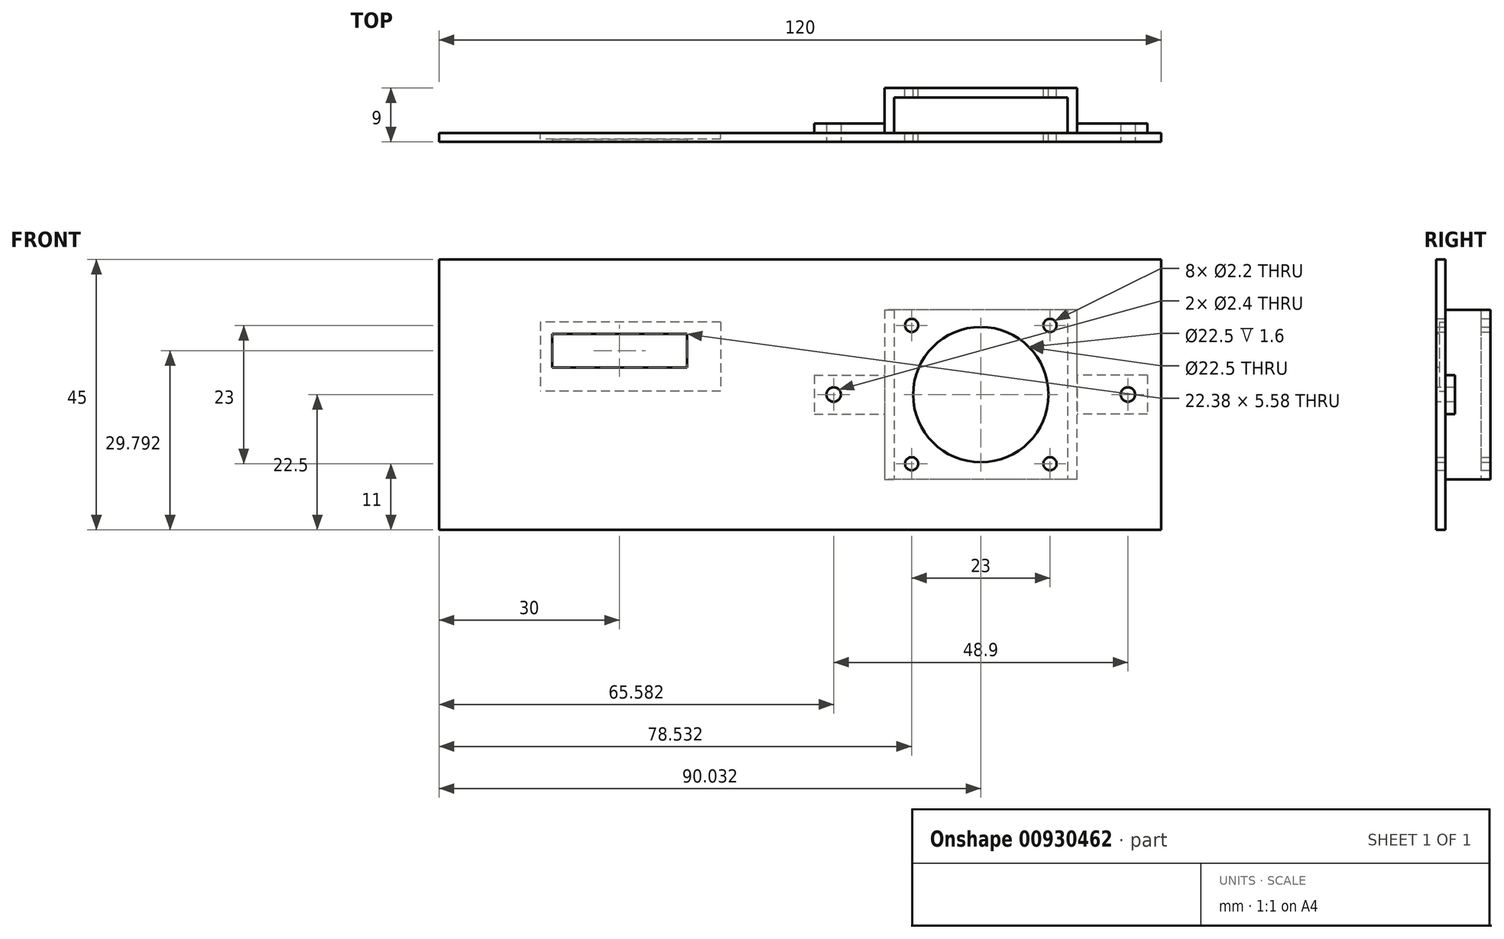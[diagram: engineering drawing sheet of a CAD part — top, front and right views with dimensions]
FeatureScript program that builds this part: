
annotation { "Feature Type Name" : "Feature", "Feature Type Description" : "" }
export const myFeature = defineFeature(function(context is Context, id is Id, definition is map)
    precondition{}
    {
        {
            var Q0;
            Q0=qCreatedBy(makeId("Top.planeOp"),FACE);
            var sketch = newSketch(context, id + "F0", { "sketchPlane" : qUnion([Q0])});
            skLineSegment(sketch, "E0.bottom", {"start": v(60, 0.75) * mm, "end": v(-60, 0.75) * mm});
            skLineSegment(sketch, "E0.top", {"start": v(60, -0.75) * mm, "end": v(-60, -0.75) * mm});
            skLineSegment(sketch, "E0.left", {"start": v(60, 0.75) * mm, "end": v(60, -0.75) * mm});
            skLineSegment(sketch, "E0.right", {"start": v(-60, 0.75) * mm, "end": v(-60, -0.75) * mm});
            skPoint(sketch, "E0.middle", {"position": v(0, 0) * mm});
            skSolve(sketch);
        }
        {
            var Q0;
            Q0 = qSketchRegion(id + "F0", true);
            extrude(context, id + "F1", {"entities" : qUnion([Q0]), "depth" : 45 * mm, "offsetDistance" : 25 * mm});
        }
        {
            var Q0;
            Q0=makeQuery(id+"F1.opExtrude","SWEPT_FACE",FACE,{"disambiguationData":[OSD([sQuery(id+"F0.wireOp",EDGE,"E0.top")])]});
            var sketch = newSketch(context, id + "F2", { "sketchPlane" : qUnion([Q0])});
            skCircle(sketch, "E1", {"center": v(30.03, 22.5) * mm, "radius": 4 * mm});
            skPoint(sketch, "E1.centerSnap0", {"position": v(60, 22.5) * mm});
            skSolve(sketch);
        }
        {
            var Q0;
            Q0=makeQuery(id+"F2.imprint","IMPRINT",FACE,{"disambiguationData":[TD([[makeQuery(id+"F2.imprint","IMPRINT",EDGE,{"derivedFrom":sQuery(id+"F2.wireOp",EDGE,"E1")}),1.0]])]});
            extrude(context, id + "F3", {"entities" : qUnion([Q0]), "operationType" : NewBodyOperationType.REMOVE, "oppositeDirection" : true, "depth" : 25 * mm, "offsetDistance" : 25 * mm});
        }
        {
            var Q0;
            Q0=makeQuery(id+"F1.opExtrude","SWEPT_FACE",FACE,{"disambiguationData":[OSD([sQuery(id+"F0.wireOp",EDGE,"E0.top")])]});
            var sketch = newSketch(context, id + "F4", { "sketchPlane" : qUnion([Q0])});
            skCircle(sketch, "E2", {"center": v(5.58, 22.5) * mm, "radius": 1.2 * mm});
            skCircle(sketch, "E3", {"center": v(54.48, 22.5) * mm, "radius": 1.2 * mm});
            skPoint(sketch, "E4", {"position": v(30.03, 22.5) * mm});
            skLineSegment(sketch, "E5", {"start": v(30.03, 26.5) * mm, "end": v(30.03, 18.5) * mm, "construction": true});
            skSolve(sketch);
        }
        {
            var Q0;
            Q0 = qSketchRegion(id + "F4", true);
            extrude(context, id + "F5", {"entities" : qUnion([Q0]), "operationType" : NewBodyOperationType.REMOVE, "oppositeDirection" : true, "depth" : 25 * mm, "offsetDistance" : 25 * mm});
        }
        {
            var Q0;
            Q0=makeQuery(id+"F1.opExtrude","SWEPT_FACE",FACE,{"disambiguationData":[OSD([sQuery(id+"F0.wireOp",EDGE,"E0.bottom")])]});
            var sketch = newSketch(context, id + "F6", { "sketchPlane" : qUnion([Q0])});
            skLineSegment(sketch, "E6.bottom", {"start": v(-57.73, 25.75) * mm, "end": v(-46.03, 25.75) * mm});
            skLineSegment(sketch, "E6.top", {"start": v(-57.73, 19.25) * mm, "end": v(-46.03, 19.25) * mm});
            skLineSegment(sketch, "E6.left", {"start": v(-57.73, 25.75) * mm, "end": v(-57.73, 19.25) * mm});
            skPoint(sketch, "E7", {"position": v(-30.03, 22.5) * mm});
            skLineSegment(sketch, "E8", {"start": v(-30.03, 26.5) * mm, "end": v(-30.03, 26.5) * mm});
            skLineSegment(sketch, "E9", {"start": v(-46.03, 25.75) * mm, "end": v(-46.03, 36.6) * mm});
            skLineSegment(sketch, "E10", {"start": v(-46.03, 36.6) * mm, "end": v(-44.43, 36.6) * mm});
            skLineSegment(sketch, "E11", {"start": v(-46.03, 19.25) * mm, "end": v(-46.03, 8.4) * mm});
            skLineSegment(sketch, "E12", {"start": v(-46.03, 8.4) * mm, "end": v(-44.43, 8.4) * mm});
            skLineSegment(sketch, "E13", {"start": v(-46.03, 25.75) * mm, "end": v(-46.03, 19.25) * mm});
            skPoint(sketch, "E14", {"position": v(-54.48, 22.5) * mm});
            skPoint(sketch, "E15", {"position": v(-57.73, 22.5) * mm});
            skLineSegment(sketch, "E16", {"start": v(-44.43, 36.6) * mm, "end": v(-44.43, 8.4) * mm});
            skLineSegment(sketch, "E17.MirrorCS", {"start": v(-14.03, 36.6) * mm, "end": v(-15.63, 36.6) * mm});
            skLineSegment(sketch, "E18.MirrorCS", {"start": v(-14.03, 8.4) * mm, "end": v(-15.63, 8.4) * mm});
            skLineSegment(sketch, "E19.MirrorCS", {"start": v(-2.33, 25.75) * mm, "end": v(-2.33, 19.25) * mm});
            skLineSegment(sketch, "E20.MirrorCS", {"start": v(-15.63, 36.6) * mm, "end": v(-15.63, 8.4) * mm});
            skPoint(sketch, "E21.MirrorP", {"position": v(-5.58, 22.5) * mm});
            skLineSegment(sketch, "E22.MirrorCS", {"start": v(-2.33, 25.75) * mm, "end": v(-14.03, 25.75) * mm});
            skPoint(sketch, "E23.MirrorP", {"position": v(-2.33, 22.5) * mm});
            skLineSegment(sketch, "E24.MirrorCS", {"start": v(-14.03, 25.75) * mm, "end": v(-14.03, 19.25) * mm});
            skLineSegment(sketch, "E25.MirrorCS", {"start": v(-14.03, 19.25) * mm, "end": v(-14.03, 8.4) * mm});
            skLineSegment(sketch, "E26.MirrorCS", {"start": v(-2.33, 19.25) * mm, "end": v(-14.03, 19.25) * mm});
            skLineSegment(sketch, "E27.MirrorCS", {"start": v(-14.03, 25.75) * mm, "end": v(-14.03, 36.6) * mm});
            skSolve(sketch);
        }
        {
            var Q0;
            Q0=makeQuery(id+"F6.imprint","IMPRINT",FACE,{"disambiguationData":[TD([[makeQuery(id+"F6.imprint","IMPRINT",EDGE,{"derivedFrom":sQuery(id+"F6.wireOp",EDGE,"E6.bottom")}),-1.0]])]});
            var Q1;
            Q1=makeQuery(id+"F6.imprint","IMPRINT",FACE,{"disambiguationData":[TD([[makeQuery(id+"F6.imprint","IMPRINT",EDGE,{"derivedFrom":sQuery(id+"F6.wireOp",EDGE,"E19.MirrorCS")}),-1.0]])]});
            extrude(context, id + "F7", {"entities" : qUnion([Q0, Q1]), "depth" : 1.6 * mm, "offsetDistance" : 25 * mm});
        }
        {
            var Q0;
            Q0=makeQuery(id+"F6.imprint","IMPRINT",FACE,{"disambiguationData":[TD([[makeQuery(id+"F6.imprint","IMPRINT",EDGE,{"derivedFrom":sQuery(id+"F6.wireOp",EDGE,"E9")}),-1.0]])]});
            var Q1;
            Q1=makeQuery(id+"F6.imprint","IMPRINT",FACE,{"disambiguationData":[TD([[makeQuery(id+"F6.imprint","IMPRINT",EDGE,{"derivedFrom":sQuery(id+"F6.wireOp",EDGE,"E17.MirrorCS")}),1.0]])]});
            extrude(context, id + "F8", {"entities" : qUnion([Q0, Q1]), "operationType" : NewBodyOperationType.ADD, "depth" : 5.9 * mm, "offsetDistance" : 25 * mm});
        }
        {
            var Q0;
            Q0=makeQuery(id+"F8.opExtrude","CAP_FACE",FACE,{"disambiguationData":[OSD([sQuery(id+"F6.wireOp",EDGE,"E9"),sQuery(id+"F6.wireOp",EDGE,"E10"),sQuery(id+"F6.wireOp",EDGE,"E11"),sQuery(id+"F6.wireOp",EDGE,"E12"),sQuery(id+"F6.wireOp",EDGE,"E13"),sQuery(id+"F6.wireOp",EDGE,"E16")])],"isStart":false});
            var sketch = newSketch(context, id + "F9", { "sketchPlane" : qUnion([Q0])});
            skLineSegment(sketch, "E28.bottom", {"start": v(-46.03, 36.6) * mm, "end": v(-14.03, 36.6) * mm});
            skLineSegment(sketch, "E28.top", {"start": v(-46.03, 8.4) * mm, "end": v(-14.03, 8.4) * mm});
            skLineSegment(sketch, "E28.left", {"start": v(-46.03, 36.6) * mm, "end": v(-46.03, 8.4) * mm});
            skLineSegment(sketch, "E28.right", {"start": v(-14.03, 36.6) * mm, "end": v(-14.03, 8.4) * mm});
            skSolve(sketch);
        }
        {
            var Q0;
            Q0 = qSketchRegion(id + "F9", true);
            extrude(context, id + "F10", {"entities" : qUnion([Q0]), "operationType" : NewBodyOperationType.ADD, "depth" : 1.6 * mm, "offsetDistance" : 25 * mm});
        }
        {
            var Q0;
            Q0=makeQuery(id+"F10.opExtrude","CAP_FACE",FACE,{"disambiguationData":[OSD([sQuery(id+"F9.wireOp",EDGE,"E28.bottom"),sQuery(id+"F9.wireOp",EDGE,"E28.top"),sQuery(id+"F9.wireOp",EDGE,"E28.left"),sQuery(id+"F9.wireOp",EDGE,"E28.right")])],"isStart":false});
            var sketch = newSketch(context, id + "F11", { "sketchPlane" : qUnion([Q0])});
            skCircle(sketch, "E29", {"center": v(-30.03, 22.5) * mm, "radius": 11.25 * mm});
            skPoint(sketch, "E29.centerSnap0", {"position": v(-14.03, 22.5) * mm});
            skPoint(sketch, "E29.centerSnap1", {"position": v(-30.03, 36.6) * mm});
            skSolve(sketch);
        }
        {
            var Q0;
            Q0 = qSketchRegion(id + "F11", true);
            extrude(context, id + "F12", {"entities" : qUnion([Q0]), "operationType" : NewBodyOperationType.REMOVE, "oppositeDirection" : true, "depth" : 25 * mm, "offsetDistance" : 25 * mm});
        }
        {
            var Q0;
            Q0=makeQuery(id+"F10.opExtrude","CAP_FACE",FACE,{"disambiguationData":[OSD([sQuery(id+"F9.wireOp",EDGE,"E28.bottom"),sQuery(id+"F9.wireOp",EDGE,"E28.top"),sQuery(id+"F9.wireOp",EDGE,"E28.left"),sQuery(id+"F9.wireOp",EDGE,"E28.right")])],"isStart":false});
            var sketch = newSketch(context, id + "F13", { "sketchPlane" : qUnion([Q0])});
            skCircle(sketch, "E30", {"center": v(-41.53, 34) * mm, "radius": 1.1 * mm});
            skLineSegment(sketch, "E31", {"start": v(-30.03, 22.5) * mm, "end": v(-30.03, 33.75) * mm, "construction": true});
            skCircle(sketch, "E32.MirrorC", {"center": v(-18.53, 34) * mm, "radius": 1.1 * mm});
            skLineSegment(sketch, "E33", {"start": v(-30.03, 22.5) * mm, "end": v(-18.78, 22.5) * mm, "construction": true});
            skCircle(sketch, "E34.MirrorC", {"center": v(-18.53, 11) * mm, "radius": 1.1 * mm});
            skCircle(sketch, "E35.MirrorC", {"center": v(-41.53, 11) * mm, "radius": 1.1 * mm});
            skSolve(sketch);
        }
        {
            var Q0;
            Q0 = qSketchRegion(id + "F13", true);
            extrude(context, id + "F14", {"entities" : qUnion([Q0]), "operationType" : NewBodyOperationType.REMOVE, "oppositeDirection" : true, "depth" : 25 * mm, "offsetDistance" : 25 * mm});
        }
        {
            var Q0;
            Q0=makeQuery(id+"F1.opExtrude","SWEPT_FACE",FACE,{"disambiguationData":[OSD([sQuery(id+"F0.wireOp",EDGE,"E0.top")])]});
            var sketch = newSketch(context, id + "F15", { "sketchPlane" : qUnion([Q0])});
            skLineSegment(sketch, "E36.bottom", {"start": v(-41.2, 32.58) * mm, "end": v(-18.8, 32.58) * mm});
            skLineSegment(sketch, "E36.top", {"start": v(-41.2, 27) * mm, "end": v(-18.8, 27) * mm});
            skLineSegment(sketch, "E36.left", {"start": v(-41.2, 32.58) * mm, "end": v(-41.2, 27) * mm});
            skLineSegment(sketch, "E36.right", {"start": v(-18.8, 32.58) * mm, "end": v(-18.8, 27) * mm});
            skLineSegment(sketch, "E37", {"start": v(-60, 22.5) * mm, "end": v(0, 22.5) * mm, "construction": true});
            skPoint(sketch, "E38", {"position": v(-30, 27) * mm});
            skPoint(sketch, "E39", {"position": v(-30, 22.5) * mm});
            skSolve(sketch);
        }
        {
            var Q0;
            Q0=makeQuery(id+"F15.imprint","IMPRINT",FACE,{"disambiguationData":[TD([[makeQuery(id+"F15.imprint","IMPRINT",EDGE,{"derivedFrom":sQuery(id+"F15.wireOp",EDGE,"E36.bottom")}),-1.0]])]});
            extrude(context, id + "F16", {"entities" : qUnion([Q0]), "operationType" : NewBodyOperationType.REMOVE, "oppositeDirection" : true, "depth" : 25 * mm, "offsetDistance" : 25 * mm});
        }
        {
            var Q0;
            Q0=makeQuery(id+"F1.opExtrude","SWEPT_FACE",FACE,{"disambiguationData":[OSD([sQuery(id+"F0.wireOp",EDGE,"E0.bottom")])]});
            var sketch = newSketch(context, id + "F17", { "sketchPlane" : qUnion([Q0])});
            skLineSegment(sketch, "E40.bottom", {"start": v(13.2, 34.58) * mm, "end": v(43.2, 34.58) * mm});
            skLineSegment(sketch, "E40.top", {"start": v(13.2, 23.08) * mm, "end": v(43.2, 23.08) * mm});
            skLineSegment(sketch, "E40.left", {"start": v(13.2, 34.58) * mm, "end": v(13.2, 23.08) * mm});
            skLineSegment(sketch, "E40.right", {"start": v(43.2, 34.58) * mm, "end": v(43.2, 23.08) * mm});
            skSolve(sketch);
        }
        {
            var Q0;
            Q0=makeQuery(id+"F17.imprint","IMPRINT",FACE,{"disambiguationData":[TD([[makeQuery(id+"F17.imprint","IMPRINT",EDGE,{"derivedFrom":sQuery(id+"F17.wireOp",EDGE,"E40.bottom")}),-1.0]])]});
            extrude(context, id + "F18", {"entities" : qUnion([Q0]), "operationType" : NewBodyOperationType.REMOVE, "oppositeDirection" : true, "depth" : 1 * mm, "offsetDistance" : 25 * mm});
        }
    });
